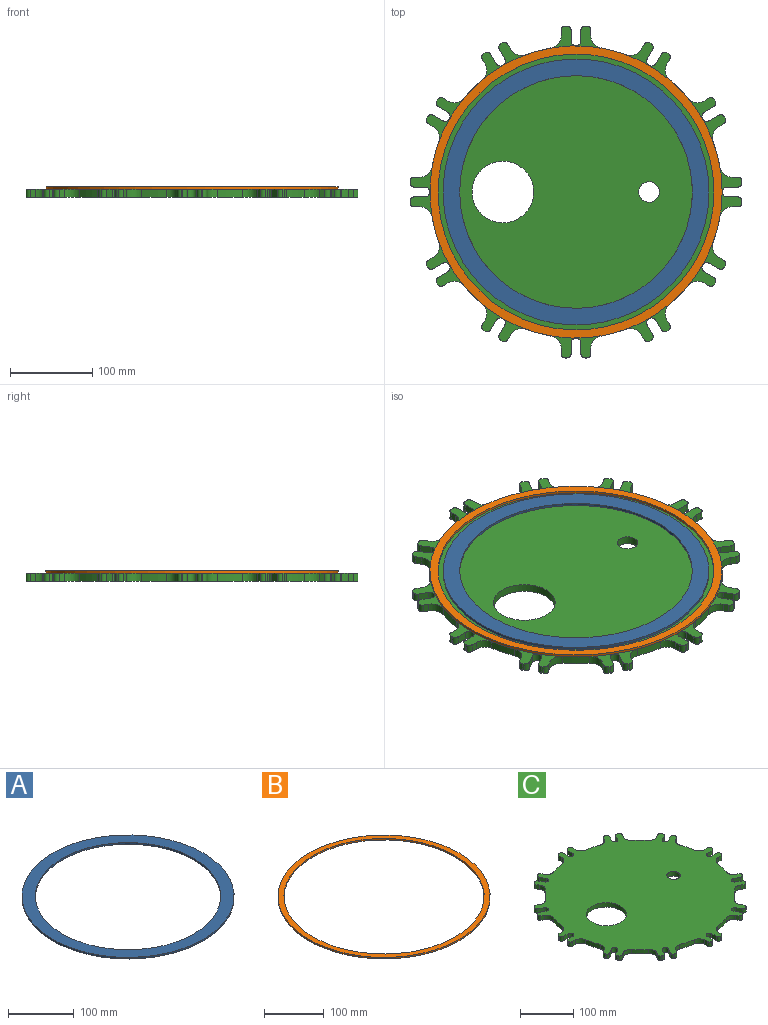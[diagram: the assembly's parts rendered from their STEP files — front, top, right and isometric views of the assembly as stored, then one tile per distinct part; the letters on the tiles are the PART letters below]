
ASSEMBLY  parts=3 mates=2
PART A: 4 faces, bbox 323x323x3 mm
  f0: cylinder r=161.5mm len=323mm, axis (0,0,-1), area 3044.2mm2, adj f1,f2
  f1: plane 323x323mm, normal (0,0,1), area 19260.1mm2, adj f0,f3
  f2: plane 323x323mm, normal (0,0,-1), area 19260.1mm2, adj f0,f3
  f3: cylinder r=141.25mm len=282.5mm, axis (0,0,-1), area 2662.5mm2, adj f1,f2
PART B: 4 faces, bbox 355x355x3 mm
  f0: cylinder r=167.5mm len=335mm, axis (0,0,-1), area 3157.3mm2, adj f2,f3
  f1: cylinder r=177.5mm len=355mm, axis (0,0,-1), area 3345.8mm2, adj f2,f3
  f2: plane 355x355mm, normal (0,0,1), area 10838.5mm2, adj f0,f1
  f3: plane 355x355mm, normal (0,0,-1), area 10838.5mm2, adj f0,f1
PART C: 172 faces, bbox 403.2x403.2x10 mm
  f0: cylinder r=177.5mm len=22.44mm, axis (0,0,-1), area 317.8mm2, adj f12,f13,f155,f169
  f1: cylinder r=177.5mm len=30.66mm, axis (0,0,-1), area 317.8mm2, adj f12,f13,f142,f156
  f2: cylinder r=177.5mm len=30.66mm, axis (0,0,-1), area 317.8mm2, adj f12,f13,f129,f143
  f3: cylinder r=177.5mm len=22.44mm, axis (0,0,-1), area 317.8mm2, adj f12,f13,f116,f130
  f4: cylinder r=177.5mm len=30.66mm, axis (0,0,-1), area 317.8mm2, adj f12,f13,f103,f117
  f5: cylinder r=177.5mm len=30.66mm, axis (0,0,-1), area 317.8mm2, adj f12,f13,f90,f104
  f6: cylinder r=177.5mm len=22.44mm, axis (0,0,-1), area 317.8mm2, adj f12,f13,f77,f91
  f7: cylinder r=177.5mm len=30.66mm, axis (0,0,-1), area 317.8mm2, adj f12,f13,f64,f78
  f8: cylinder r=177.5mm len=30.66mm, axis (0,0,-1), area 317.8mm2, adj f12,f13,f51,f65
  f9: cylinder r=177.5mm len=22.44mm, axis (0,0,-1), area 317.8mm2, adj f12,f13,f38,f52
  f10: cylinder r=177.5mm len=30.66mm, axis (0,0,-1), area 317.8mm2, adj f12,f13,f25,f39
  f11: cylinder r=177.5mm len=30.66mm, axis (0,0,-1), area 317.8mm2, adj f12,f13,f26,f168
  f12: plane 403.17x403.17mm, normal (0,0,1), area 101877.4mm2, adj f0,f1,f2,f3,f4,f5,f6,f7
  f13: plane 403.17x403.17mm, normal (0,0,-1), area 101877.4mm2, adj f0,f1,f2,f3,f4,f5,f6,f7
  f14: plane 10x6.93mm, normal (1,0,0), area 69.3mm2, adj f12,f13,f15,f26
  f15: cylinder r=5mm len=10mm, axis (0,0,-1), area 78.5mm2, adj f12,f13,f14,f16
  f16: plane 10x2mm, normal (0,1,0), area 20mm2, adj f12,f13,f15,f17
  f17: cylinder r=5mm len=10mm, axis (0,0,-1), area 78.5mm2, adj f12,f13,f16,f18
  f18: plane 13.09x10mm, normal (-1,0,0), area 130.8mm2, adj f12,f13,f17,f19
  f19: cylinder r=6mm len=12mm, axis (0,0,-1), area 188.5mm2, adj f12,f13,f18,f20
  f20: plane 13.09x10mm, normal (1,0,0), area 130.8mm2, adj f12,f13,f19,f21
  f21: cylinder r=5mm len=10mm, axis (0,0,-1), area 78.5mm2, adj f12,f13,f20,f22
  f22: plane 10x2mm, normal (0,1,0), area 20mm2, adj f12,f13,f21,f23
  f23: cylinder r=5mm len=10mm, axis (0,0,-1), area 78.5mm2, adj f12,f13,f22,f24
  f24: plane 10x6.93mm, normal (-1,0,0), area 69.3mm2, adj f12,f13,f23,f25
  f25: cylinder r=15mm len=14.78mm, axis (0,0,-1), area 209.8mm2, adj f10,f12,f13,f24
  f26: cylinder r=15mm len=14.78mm, axis (0,0,-1), area 209.8mm2, adj f11,f12,f13,f14
  f27: plane 10x6.01mm, normal (0.87,0.5,0), area 69.3mm2, adj f12,f13,f28,f39
  f28: cylinder r=5mm len=10mm, axis (0,0,-1), area 78.5mm2, adj f12,f13,f27,f29
  f29: plane 10x1.73mm, normal (-0.5,0.87,0), area 20mm2, adj f12,f13,f28,f30
  f30: cylinder r=5mm len=10mm, axis (0,0,-1), area 78.5mm2, adj f12,f13,f29,f31
  f31: plane 11.33x10mm, normal (-0.87,-0.5,0), area 130.8mm2, adj f12,f13,f30,f32
  f32: cylinder r=6mm len=11.2mm, axis (0,0,-1), area 188.5mm2, adj f12,f13,f31,f33
  f33: plane 11.33x10mm, normal (0.87,0.5,0), area 130.8mm2, adj f12,f13,f32,f34
  f34: cylinder r=5mm len=10mm, axis (0,0,-1), area 78.5mm2, adj f12,f13,f33,f35
  f35: plane 10x1.73mm, normal (-0.5,0.87,0), area 20mm2, adj f12,f13,f34,f36
  f36: cylinder r=5mm len=10mm, axis (0,0,-1), area 78.5mm2, adj f12,f13,f35,f37
  f37: plane 10x6.01mm, normal (-0.87,-0.5,0), area 69.3mm2, adj f12,f13,f36,f38
  f38: cylinder r=15mm len=19.01mm, axis (0,0,-1), area 209.8mm2, adj f9,f12,f13,f37
  f39: cylinder r=15mm len=18.15mm, axis (0,0,-1), area 209.8mm2, adj f10,f12,f13,f27
  f40: plane 10x6.01mm, normal (0.5,0.87,0), area 69.3mm2, adj f12,f13,f41,f52
  f41: cylinder r=5mm len=10mm, axis (0,0,-1), area 78.5mm2, adj f12,f13,f40,f42
  f42: plane 10x1.73mm, normal (-0.87,0.5,0), area 20mm2, adj f12,f13,f41,f43
  f43: cylinder r=5mm len=10mm, axis (0,0,-1), area 78.5mm2, adj f12,f13,f42,f44
  f44: plane 11.33x10mm, normal (-0.5,-0.87,0), area 130.8mm2, adj f12,f13,f43,f45
  f45: cylinder r=6mm len=11.2mm, axis (0,0,-1), area 188.5mm2, adj f12,f13,f44,f46
  f46: plane 11.33x10mm, normal (0.5,0.87,0), area 130.8mm2, adj f12,f13,f45,f47
  f47: cylinder r=5mm len=10mm, axis (0,0,-1), area 78.5mm2, adj f12,f13,f46,f48
  f48: plane 10x1.73mm, normal (-0.87,0.5,0), area 20mm2, adj f12,f13,f47,f49
  f49: cylinder r=5mm len=10mm, axis (0,0,-1), area 78.5mm2, adj f12,f13,f48,f50
  f50: plane 10x6.01mm, normal (-0.5,-0.87,0), area 69.3mm2, adj f12,f13,f49,f51
  f51: cylinder r=15mm len=18.15mm, axis (0,0,-1), area 209.8mm2, adj f8,f12,f13,f50
  f52: cylinder r=15mm len=19.01mm, axis (0,0,-1), area 209.8mm2, adj f9,f12,f13,f40
  f53: plane 10x6.93mm, normal (0,1,0), area 69.3mm2, adj f12,f13,f54,f65
  f54: cylinder r=5mm len=10mm, axis (0,0,-1), area 78.5mm2, adj f12,f13,f53,f55
  f55: plane 10x2mm, normal (-1,0,0), area 20mm2, adj f12,f13,f54,f56
  f56: cylinder r=5mm len=10mm, axis (0,0,-1), area 78.5mm2, adj f12,f13,f55,f57
  f57: plane 13.09x10mm, normal (0,-1,0), area 130.8mm2, adj f12,f13,f56,f58
  f58: cylinder r=6mm len=12mm, axis (0,0,-1), area 188.5mm2, adj f12,f13,f57,f59
  f59: plane 13.09x10mm, normal (0,1,0), area 130.8mm2, adj f12,f13,f58,f60
  f60: cylinder r=5mm len=10mm, axis (0,0,-1), area 78.5mm2, adj f12,f13,f59,f61
  f61: plane 10x2mm, normal (-1,0,0), area 20mm2, adj f12,f13,f60,f62
  f62: cylinder r=5mm len=10mm, axis (0,0,-1), area 78.5mm2, adj f12,f13,f61,f63
  f63: plane 10x6.93mm, normal (0,-1,0), area 69.3mm2, adj f12,f13,f62,f64
  f64: cylinder r=15mm len=14.78mm, axis (0,0,-1), area 209.8mm2, adj f7,f12,f13,f63
  f65: cylinder r=15mm len=14.78mm, axis (0,0,-1), area 209.8mm2, adj f8,f12,f13,f53
  f66: plane 10x6.01mm, normal (-0.5,0.87,0), area 69.3mm2, adj f12,f13,f67,f78
  f67: cylinder r=5mm len=10mm, axis (0,0,-1), area 78.5mm2, adj f12,f13,f66,f68
  f68: plane 10x1.73mm, normal (-0.87,-0.5,0), area 20mm2, adj f12,f13,f67,f69
  f69: cylinder r=5mm len=10mm, axis (0,0,-1), area 78.5mm2, adj f12,f13,f68,f70
  f70: plane 11.33x10mm, normal (0.5,-0.87,0), area 130.8mm2, adj f12,f13,f69,f71
  f71: cylinder r=6mm len=11.2mm, axis (0,0,-1), area 188.5mm2, adj f12,f13,f70,f72
  f72: plane 11.33x10mm, normal (-0.5,0.87,0), area 130.8mm2, adj f12,f13,f71,f73
  f73: cylinder r=5mm len=10mm, axis (0,0,-1), area 78.5mm2, adj f12,f13,f72,f74
  f74: plane 10x1.73mm, normal (-0.87,-0.5,0), area 20mm2, adj f12,f13,f73,f75
  f75: cylinder r=5mm len=10mm, axis (0,0,-1), area 78.5mm2, adj f12,f13,f74,f76
  f76: plane 10x6.01mm, normal (0.5,-0.87,0), area 69.3mm2, adj f12,f13,f75,f77
  f77: cylinder r=15mm len=19.01mm, axis (0,0,-1), area 209.8mm2, adj f6,f12,f13,f76
  f78: cylinder r=15mm len=18.15mm, axis (0,0,-1), area 209.8mm2, adj f7,f12,f13,f66
  f79: plane 10x6.01mm, normal (-0.87,0.5,0), area 69.3mm2, adj f12,f13,f80,f91
  f80: cylinder r=5mm len=10mm, axis (0,0,-1), area 78.5mm2, adj f12,f13,f79,f81
  f81: plane 10x1.73mm, normal (-0.5,-0.87,0), area 20mm2, adj f12,f13,f80,f82
  f82: cylinder r=5mm len=10mm, axis (0,0,-1), area 78.5mm2, adj f12,f13,f81,f83
  f83: plane 11.33x10mm, normal (0.87,-0.5,0), area 130.8mm2, adj f12,f13,f82,f84
  f84: cylinder r=6mm len=11.2mm, axis (0,0,-1), area 188.5mm2, adj f12,f13,f83,f85
  f85: plane 11.33x10mm, normal (-0.87,0.5,0), area 130.8mm2, adj f12,f13,f84,f86
  f86: cylinder r=5mm len=10mm, axis (0,0,-1), area 78.5mm2, adj f12,f13,f85,f87
  f87: plane 10x1.73mm, normal (-0.5,-0.87,0), area 20mm2, adj f12,f13,f86,f88
  f88: cylinder r=5mm len=10mm, axis (0,0,-1), area 78.5mm2, adj f12,f13,f87,f89
  f89: plane 10x6.01mm, normal (0.87,-0.5,0), area 69.3mm2, adj f12,f13,f88,f90
  f90: cylinder r=15mm len=18.15mm, axis (0,0,-1), area 209.8mm2, adj f5,f12,f13,f89
  f91: cylinder r=15mm len=19.01mm, axis (0,0,-1), area 209.8mm2, adj f6,f12,f13,f79
  f92: plane 10x6.93mm, normal (-1,0,0), area 69.3mm2, adj f12,f13,f93,f104
  f93: cylinder r=5mm len=10mm, axis (0,0,-1), area 78.5mm2, adj f12,f13,f92,f94
  f94: plane 10x2mm, normal (0,-1,0), area 20mm2, adj f12,f13,f93,f95
  f95: cylinder r=5mm len=10mm, axis (0,0,-1), area 78.5mm2, adj f12,f13,f94,f96
  f96: plane 13.09x10mm, normal (1,0,0), area 130.8mm2, adj f12,f13,f95,f97
  f97: cylinder r=6mm len=12mm, axis (0,0,-1), area 188.5mm2, adj f12,f13,f96,f98
  f98: plane 13.09x10mm, normal (-1,0,0), area 130.8mm2, adj f12,f13,f97,f99
  f99: cylinder r=5mm len=10mm, axis (0,0,-1), area 78.5mm2, adj f12,f13,f98,f100
  f100: plane 10x2mm, normal (0,-1,0), area 20mm2, adj f12,f13,f99,f101
  f101: cylinder r=5mm len=10mm, axis (0,0,-1), area 78.5mm2, adj f12,f13,f100,f102
  f102: plane 10x6.93mm, normal (1,0,0), area 69.3mm2, adj f12,f13,f101,f103
  f103: cylinder r=15mm len=14.78mm, axis (0,0,-1), area 209.8mm2, adj f4,f12,f13,f102
  f104: cylinder r=15mm len=14.78mm, axis (0,0,-1), area 209.8mm2, adj f5,f12,f13,f92
  f105: plane 10x6.01mm, normal (-0.87,-0.5,0), area 69.3mm2, adj f12,f13,f106,f117
  f106: cylinder r=5mm len=10mm, axis (0,0,-1), area 78.5mm2, adj f12,f13,f105,f107
  f107: plane 10x1.73mm, normal (0.5,-0.87,0), area 20mm2, adj f12,f13,f106,f108
  f108: cylinder r=5mm len=10mm, axis (0,0,-1), area 78.5mm2, adj f12,f13,f107,f109
  f109: plane 11.33x10mm, normal (0.87,0.5,0), area 130.8mm2, adj f12,f13,f108,f110
  f110: cylinder r=6mm len=11.2mm, axis (0,0,-1), area 188.5mm2, adj f12,f13,f109,f111
  f111: plane 11.33x10mm, normal (-0.87,-0.5,0), area 130.8mm2, adj f12,f13,f110,f112
  f112: cylinder r=5mm len=10mm, axis (0,0,-1), area 78.5mm2, adj f12,f13,f111,f113
  f113: plane 10x1.73mm, normal (0.5,-0.87,0), area 20mm2, adj f12,f13,f112,f114
  f114: cylinder r=5mm len=10mm, axis (0,0,-1), area 78.5mm2, adj f12,f13,f113,f115
  f115: plane 10x6.01mm, normal (0.87,0.5,0), area 69.3mm2, adj f12,f13,f114,f116
  f116: cylinder r=15mm len=19.01mm, axis (0,0,-1), area 209.8mm2, adj f3,f12,f13,f115
  f117: cylinder r=15mm len=18.15mm, axis (0,0,-1), area 209.8mm2, adj f4,f12,f13,f105
  f118: plane 10x6.01mm, normal (-0.5,-0.87,0), area 69.3mm2, adj f12,f13,f119,f130
  f119: cylinder r=5mm len=10mm, axis (0,0,-1), area 78.5mm2, adj f12,f13,f118,f120
  f120: plane 10x1.73mm, normal (0.87,-0.5,0), area 20mm2, adj f12,f13,f119,f121
  f121: cylinder r=5mm len=10mm, axis (0,0,-1), area 78.5mm2, adj f12,f13,f120,f122
  f122: plane 11.33x10mm, normal (0.5,0.87,0), area 130.8mm2, adj f12,f13,f121,f123
  f123: cylinder r=6mm len=11.2mm, axis (0,0,-1), area 188.5mm2, adj f12,f13,f122,f124
  f124: plane 11.33x10mm, normal (-0.5,-0.87,0), area 130.8mm2, adj f12,f13,f123,f125
  f125: cylinder r=5mm len=10mm, axis (0,0,-1), area 78.5mm2, adj f12,f13,f124,f126
  f126: plane 10x1.73mm, normal (0.87,-0.5,0), area 20mm2, adj f12,f13,f125,f127
  f127: cylinder r=5mm len=10mm, axis (0,0,-1), area 78.5mm2, adj f12,f13,f126,f128
  f128: plane 10x6.01mm, normal (0.5,0.87,0), area 69.3mm2, adj f12,f13,f127,f129
  f129: cylinder r=15mm len=18.15mm, axis (0,0,-1), area 209.8mm2, adj f2,f12,f13,f128
  f130: cylinder r=15mm len=19.01mm, axis (0,0,-1), area 209.8mm2, adj f3,f12,f13,f118
  f131: plane 10x6.93mm, normal (0,-1,0), area 69.3mm2, adj f12,f13,f132,f143
  f132: cylinder r=5mm len=10mm, axis (0,0,-1), area 78.5mm2, adj f12,f13,f131,f133
  f133: plane 10x2mm, normal (1,0,0), area 20mm2, adj f12,f13,f132,f134
  f134: cylinder r=5mm len=10mm, axis (0,0,-1), area 78.5mm2, adj f12,f13,f133,f135
  f135: plane 13.09x10mm, normal (0,1,0), area 130.8mm2, adj f12,f13,f134,f136
  f136: cylinder r=6mm len=12mm, axis (0,0,-1), area 188.5mm2, adj f12,f13,f135,f137
  f137: plane 13.09x10mm, normal (0,-1,0), area 130.8mm2, adj f12,f13,f136,f138
  f138: cylinder r=5mm len=10mm, axis (0,0,-1), area 78.5mm2, adj f12,f13,f137,f139
  f139: plane 10x2mm, normal (1,0,0), area 20mm2, adj f12,f13,f138,f140
  f140: cylinder r=5mm len=10mm, axis (0,0,-1), area 78.5mm2, adj f12,f13,f139,f141
  f141: plane 10x6.93mm, normal (0,1,0), area 69.3mm2, adj f12,f13,f140,f142
  f142: cylinder r=15mm len=14.78mm, axis (0,0,-1), area 209.8mm2, adj f1,f12,f13,f141
  f143: cylinder r=15mm len=14.78mm, axis (0,0,-1), area 209.8mm2, adj f2,f12,f13,f131
  f144: plane 10x6.01mm, normal (0.5,-0.87,0), area 69.3mm2, adj f12,f13,f145,f156
  f145: cylinder r=5mm len=10mm, axis (0,0,-1), area 78.5mm2, adj f12,f13,f144,f146
  f146: plane 10x1.73mm, normal (0.87,0.5,0), area 20mm2, adj f12,f13,f145,f147
  f147: cylinder r=5mm len=10mm, axis (0,0,-1), area 78.5mm2, adj f12,f13,f146,f148
  f148: plane 11.33x10mm, normal (-0.5,0.87,0), area 130.8mm2, adj f12,f13,f147,f149
  f149: cylinder r=6mm len=11.2mm, axis (0,0,-1), area 188.5mm2, adj f12,f13,f148,f150
  f150: plane 11.33x10mm, normal (0.5,-0.87,0), area 130.8mm2, adj f12,f13,f149,f151
  f151: cylinder r=5mm len=10mm, axis (0,0,-1), area 78.5mm2, adj f12,f13,f150,f152
  f152: plane 10x1.73mm, normal (0.87,0.5,0), area 20mm2, adj f12,f13,f151,f153
  f153: cylinder r=5mm len=10mm, axis (0,0,-1), area 78.5mm2, adj f12,f13,f152,f154
  f154: plane 10x6.01mm, normal (-0.5,0.87,0), area 69.3mm2, adj f12,f13,f153,f155
  f155: cylinder r=15mm len=19.01mm, axis (0,0,-1), area 209.8mm2, adj f0,f12,f13,f154
  f156: cylinder r=15mm len=18.15mm, axis (0,0,-1), area 209.8mm2, adj f1,f12,f13,f144
  f157: plane 10x6.01mm, normal (0.87,-0.5,0), area 69.3mm2, adj f12,f13,f158,f169
  f158: cylinder r=5mm len=10mm, axis (0,0,-1), area 78.5mm2, adj f12,f13,f157,f159
  f159: plane 10x1.73mm, normal (0.5,0.87,0), area 20mm2, adj f12,f13,f158,f160
  f160: cylinder r=5mm len=10mm, axis (0,0,-1), area 78.5mm2, adj f12,f13,f159,f161
  f161: plane 11.33x10mm, normal (-0.87,0.5,0), area 130.8mm2, adj f12,f13,f160,f162
  f162: cylinder r=6mm len=11.2mm, axis (0,0,-1), area 188.5mm2, adj f12,f13,f161,f163
  f163: plane 11.33x10mm, normal (0.87,-0.5,0), area 130.8mm2, adj f12,f13,f162,f164
  f164: cylinder r=5mm len=10mm, axis (0,0,-1), area 78.5mm2, adj f12,f13,f163,f165
  f165: plane 10x1.73mm, normal (0.5,0.87,0), area 20mm2, adj f12,f13,f164,f166
  f166: cylinder r=5mm len=10mm, axis (0,0,-1), area 78.5mm2, adj f12,f13,f165,f167
  f167: plane 10x6.01mm, normal (-0.87,0.5,0), area 69.3mm2, adj f12,f13,f166,f168
  f168: cylinder r=15mm len=18.15mm, axis (0,0,-1), area 209.8mm2, adj f11,f12,f13,f167
  f169: cylinder r=15mm len=19.01mm, axis (0,0,-1), area 209.8mm2, adj f0,f12,f13,f157
  f170: cylinder r=12.5mm len=25mm, axis (0,0,1), area 785.4mm2, adj f12,f13
  f171: cylinder r=37.5mm len=75mm, axis (0,0,1), area 2356.2mm2, adj f12,f13
PLACE A rot(axis=(1,0,0),180deg) t=(-2.92,266.29,3.47)mm
PLACE B t=(-2.92,266.29,0.47)mm
PLACE C t=(-2.92,266.29,-9.53)mm
MATE fastened A.f0 <-> C.f0  axis (0,0,-1) through (-2.92,266.29,0.47)mm
MATE fastened B.f0 <-> C.f0  axis (0,0,-1) through (-2.92,266.29,0.47)mm
